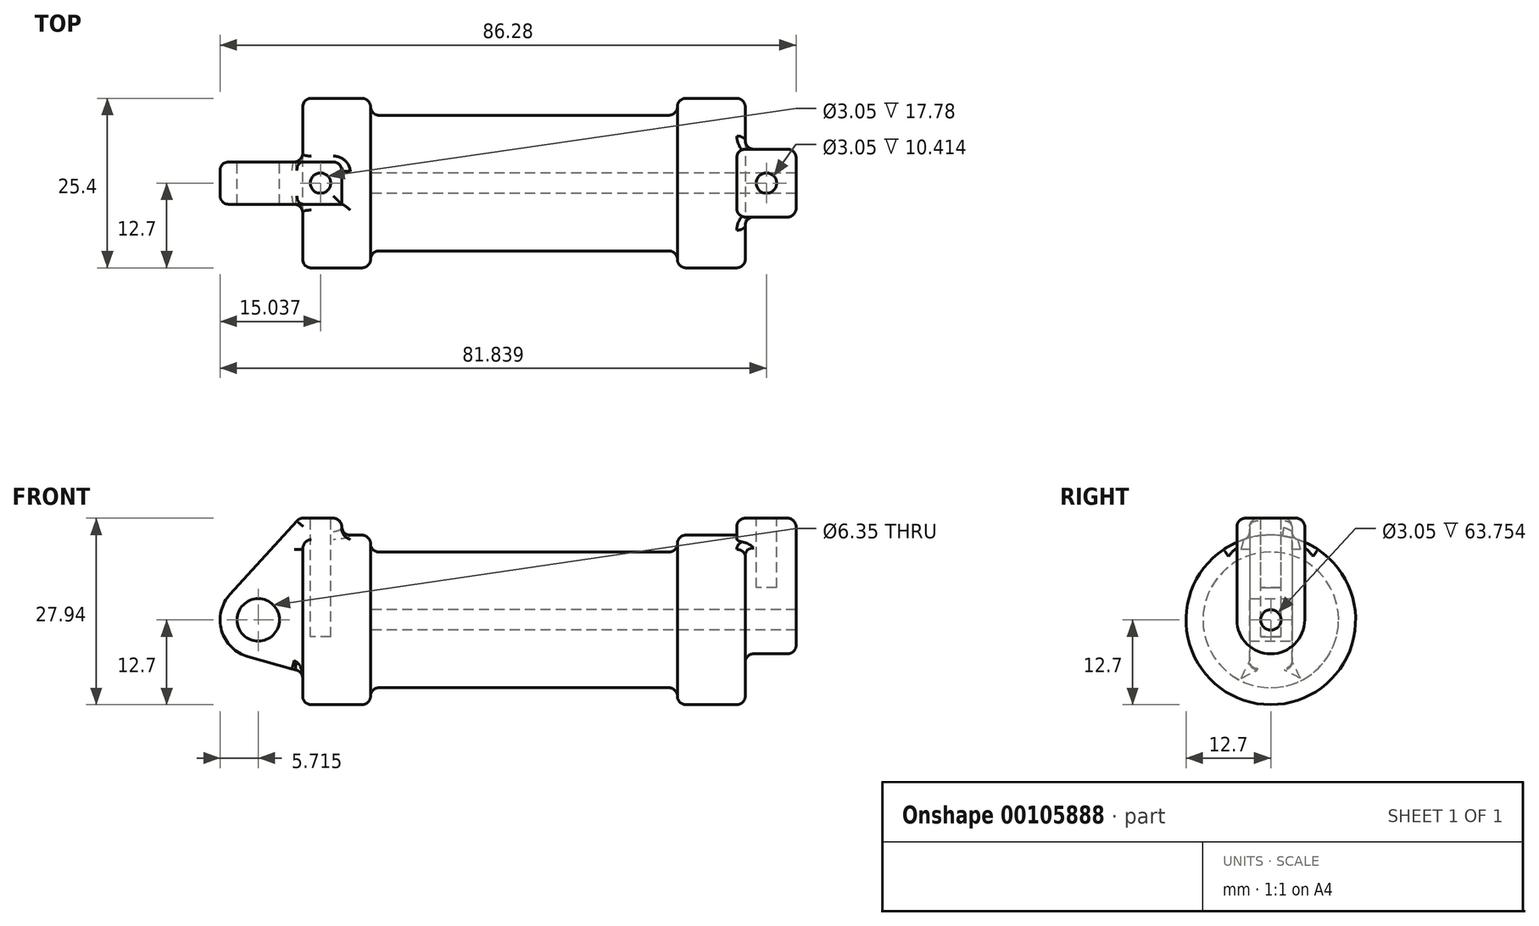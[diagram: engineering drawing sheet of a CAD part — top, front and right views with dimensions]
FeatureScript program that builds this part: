
annotation { "Feature Type Name" : "Feature", "Feature Type Description" : "" }
export const myFeature = defineFeature(function(context is Context, id is Id, definition is map)
    precondition{}
    {
        {
            var Q0;
            Q0=qCreatedBy(makeId("Front.planeOp"),FACE);
            var sketch = newSketch(context, id + "F0", { "sketchPlane" : qUnion([Q0])});
            skLineSegment(sketch, "E0", {"start": v(0, 0) * mm, "end": v(0, 12.7) * mm});
            skLineSegment(sketch, "E1", {"start": v(0, 12.7) * mm, "end": v(10.16, 12.7) * mm});
            skLineSegment(sketch, "E2", {"start": v(10.16, 12.7) * mm, "end": v(10.16, 10.16) * mm});
            skLineSegment(sketch, "E3", {"start": v(10.16, 10.16) * mm, "end": v(56.13, 10.16) * mm});
            skLineSegment(sketch, "E4", {"start": v(56.13, 10.16) * mm, "end": v(56.13, 12.7) * mm});
            skLineSegment(sketch, "E5", {"start": v(56.13, 12.7) * mm, "end": v(66.3, 12.7) * mm});
            skLineSegment(sketch, "E6", {"start": v(66.3, 12.7) * mm, "end": v(66.3, 0) * mm});
            skLineSegment(sketch, "E7", {"start": v(66.3, 0) * mm, "end": v(0, 0) * mm});
            skLineSegment(sketch, "E8", {"start": v(5.84, 15.24) * mm, "end": v(-0.5, 15.24) * mm});
            skLineSegment(sketch, "E9", {"start": v(-0.5, 15.24) * mm, "end": v(-10.88, 3.85) * mm});
            skLineSegment(sketch, "E10", {"start": v(0, 0) * mm, "end": v(-6.65, 0) * mm});
            skCircle(sketch, "E11", {"center": v(-6.65, 0) * mm, "radius": 5.72 * mm});
            skCircle(sketch, "E12", {"center": v(-6.65, 0) * mm, "radius": 3.18 * mm});
            skLineSegment(sketch, "E13", {"start": v(5.84, 15.24) * mm, "end": v(5.84, -9.4) * mm});
            skLineSegment(sketch, "E14", {"start": v(5.84, -9.4) * mm, "end": v(-8.18, -5.5) * mm});
            skSolve(sketch);
        }
        {
            var Q0;
            {var subQ0=sQuery(id+"F0.wireOp",EDGE,"E2");Q0=makeQuery(id+"F0.imprint","IMPRINT",FACE,{"disambiguationData":[TD([[makeQuery(id+"F0.imprint","IMPRINT",EDGE,{"derivedFrom":subQ0}),-1.0]])]});}
            var Q1;
            {var subQ0=sQuery(id+"F0.wireOp",EDGE,"E0");Q1=makeQuery(id+"F0.imprint","IMPRINT",FACE,{"disambiguationData":[TD([[makeQuery(id+"F0.imprint","IMPRINT",EDGE,{"derivedFrom":subQ0}),-1.0]])]});}
            var Q2;
            Q2=sQuery(id+"F0.wireOp",EDGE,"E7");
            revolve(context, id + "F1", {"entities" : qUnion([Q0, Q1]), "axis" : qUnion([Q2]), "revolveType" : RevolveType.FULL});
        }
        {
            var Q0;
            {var subQ3=sQuery(id+"F0.wireOp",EDGE,"E0");Q0=makeQuery(id+"F0.imprint","IMPRINT",FACE,{"disambiguationData":[TD([[makeQuery(id+"F0.imprint","IMPRINT",EDGE,{"derivedFrom":subQ3}),1.0]])]});}
            var Q1;
            {var subQ0=sQuery(id+"F0.wireOp",EDGE,"E0");Q1=makeQuery(id+"F0.imprint","IMPRINT",FACE,{"disambiguationData":[TD([[makeQuery(id+"F0.imprint","IMPRINT",EDGE,{"derivedFrom":subQ0}),-1.0]])]});}
            var Q2;
            {var subQ0=sQuery(id+"F0.wireOp",EDGE,"E14");Q2=makeQuery(id+"F0.imprint","IMPRINT",FACE,{"disambiguationData":[TD([[makeQuery(id+"F0.imprint","IMPRINT",EDGE,{"derivedFrom":subQ0}),-1.0]])]});}
            var Q3;
            {var subQ4=sQuery(id+"F0.wireOp",EDGE,"E12");Q3=makeQuery(id+"F0.imprint","IMPRINT",FACE,{"disambiguationData":[TD([[makeQuery(id+"F0.imprint","IMPRINT",EDGE,{"derivedFrom":subQ4}),-1.0]])]});}
            extrude(context, id + "F2", {"entities" : qUnion([Q0, Q1, Q2, Q3]), "operationType" : NewBodyOperationType.ADD, "endBound" : BoundingType.SYMMETRIC, "depth" : 6.35 * mm});
        }
        {
            var Q0;
            Q0=makeQuery(id+"F1.opRevolve","SWEPT_FACE",FACE,{"disambiguationData":[OSD([sQuery(id+"F0.wireOp",EDGE,"E6")])]});
            var sketch = newSketch(context, id + "F3", { "sketchPlane" : qUnion([Q0])});
            skCircle(sketch, "E15", {"center": v(0, 0) * mm, "radius": 1.52 * mm});
            skCircle(sketch, "E16", {"center": v(0, 0) * mm, "radius": 5.08 * mm});
            skLineSegment(sketch, "E17", {"start": v(5.08, 0) * mm, "end": v(5.08, 15.23) * mm});
            skLineSegment(sketch, "E18", {"start": v(-5.08, 0) * mm, "end": v(-5.08, 15.23) * mm});
            skLineSegment(sketch, "E19", {"start": v(-5.08, 15.23) * mm, "end": v(5.08, 15.23) * mm});
            skSolve(sketch);
        }
        {
            var Q0;
            {var subQ0=sQuery(id+"F3.wireOp",EDGE,"E19");Q0=makeQuery(id+"F3.imprint","IMPRINT",FACE,{"disambiguationData":[TD([[makeQuery(id+"F3.imprint","IMPRINT",EDGE,{"derivedFrom":subQ0}),-1.0]])]});}
            var Q1;
            {var subQ0=sQuery(id+"F3.wireOp",EDGE,"E17");var subQ1=sQuery(id+"F3.wireOp",EDGE,"E16");var subQ2=makeQuery(id+"F3.imprint","INTERSECT",VERTEX,{"derivedFrom":[subQ1,subQ0]});Q1=makeQuery(id+"F3.imprint","IMPRINT",FACE,{"disambiguationData":[TD([[makeQuery(id+"F3.imprint","IMPRINT",EDGE,{"disambiguationData":[TD([[subQ2,-1.0]])],"derivedFrom":subQ1}),-1.0]])]});}
            var Q2;
            Q2=makeQuery(id+"F3.imprint","IMPRINT",FACE,{"disambiguationData":[TD([[makeQuery(id+"F3.imprint","IMPRINT",EDGE,{"derivedFrom":sQuery(id+"F3.wireOp",EDGE,"E15")}),-1.0]])]});
            extrude(context, id + "F4", {"entities" : qUnion([Q0, Q1, Q2]), "operationType" : NewBodyOperationType.ADD, "depth" : 7.62 * mm});
        }
        {
            var Q0;
            Q0=makeQuery(id+"F4.opExtrude","CAP_FACE",FACE,{"disambiguationData":[OSD([sQuery(id+"F3.wireOp",EDGE,"E15"),sQuery(id+"F3.wireOp",EDGE,"E16"),sQuery(id+"F3.wireOp",EDGE,"E17"),sQuery(id+"F3.wireOp",EDGE,"E18"),sQuery(id+"F3.wireOp",EDGE,"E19")])],"isStart":true});
            extrude(context, id + "F5", {"entities" : qUnion([Q0]), "operationType" : NewBodyOperationType.ADD, "depth" : 1.27 * mm});
        }
        {
            var Q0;
            Q0=makeQuery(id+"F4.boolean.opBoolean","SPLIT",FACE,{"disambiguationData":[TD([makeQuery(id+"F4.opExtrude","SWEPT_FACE",FACE,{"disambiguationData":[OSD([sQuery(id+"F3.wireOp",EDGE,"E15")])]})])],"derivedFrom":makeQuery(id+"F1.opRevolve","SWEPT_FACE",FACE,{"disambiguationData":[OSD([sQuery(id+"F0.wireOp",EDGE,"E6")])]})});
            var Q1;
            Q1=makeQuery(id+"F1.opRevolve","SWEPT_FACE",FACE,{"disambiguationData":[OSD([sQuery(id+"F0.wireOp",EDGE,"E2")])]});
            extrude(context, id + "F6", {"entities" : qUnion([Q0]), "operationType" : NewBodyOperationType.REMOVE, "endBound" : BoundingType.UP_TO_SURFACE, "oppositeDirection" : true, "endBoundEntityFace" : qUnion([Q1]), "depth" : 25.4 * mm});
        }
        {
            var Q0;
            Q0=makeQuery(id+"F2.opExtrude","SWEPT_FACE",FACE,{"disambiguationData":[OSD([sQuery(id+"F0.wireOp",EDGE,"E8")])]});
            var sketch = newSketch(context, id + "F7", { "sketchPlane" : qUnion([Q0])});
            skCircle(sketch, "E20", {"center": v(2.67, 0) * mm, "radius": 1.52 * mm});
            skSolve(sketch);
        }
        {
            var Q0;
            {var subQ0=sQuery(id+"F3.wireOp",EDGE,"E19");Q0=makeQuery(id+"F5.boolean.opBoolean","MERGE",FACE,{"derivedFrom":[makeQuery(id+"F4.opExtrude","SWEPT_FACE",FACE,{"disambiguationData":[OSD([subQ0])]}),makeQuery(id+"F5.opExtrude","SWEPT_FACE",FACE,{"disambiguationData":[OSD([subQ0])]})]});}
            var sketch = newSketch(context, id + "F8", { "sketchPlane" : qUnion([Q0])});
            skCircle(sketch, "E21", {"center": v(69.47, 0) * mm, "radius": 1.52 * mm});
            skSolve(sketch);
        }
        {
            var Q0;
            Q0=makeQuery(id+"F7.imprint","IMPRINT",FACE,{"disambiguationData":[TD([[makeQuery(id+"F7.imprint","IMPRINT",EDGE,{"derivedFrom":sQuery(id+"F7.wireOp",EDGE,"E20")}),1.0]])]});
            extrude(context, id + "F9", {"entities" : qUnion([Q0]), "operationType" : NewBodyOperationType.REMOVE, "oppositeDirection" : true, "depth" : 17.78 * mm});
        }
        {
            var Q0;
            Q0=makeQuery(id+"F8.imprint","IMPRINT",FACE,{"disambiguationData":[TD([[makeQuery(id+"F8.imprint","IMPRINT",EDGE,{"derivedFrom":sQuery(id+"F8.wireOp",EDGE,"E21")}),1.0]])]});
            extrude(context, id + "F10", {"entities" : qUnion([Q0]), "operationType" : NewBodyOperationType.REMOVE, "oppositeDirection" : true, "depth" : 10.4 * mm});
        }
        {
            var Q0;
            Q0=makeQuery(id+"F1.opRevolve","SWEPT_EDGE",EDGE,{"disambiguationData":[OSD([sQuery(id+"F0.wireOp",EDGE,"E1"),sQuery(id+"F0.wireOp",EDGE,"E2")])]});
            var Q1;
            Q1=makeQuery(id+"F1.opRevolve","SWEPT_EDGE",EDGE,{"disambiguationData":[OSD([sQuery(id+"F0.wireOp",EDGE,"E2"),sQuery(id+"F0.wireOp",EDGE,"E3")])]});
            fillet(context, id + "F11", {"entities" : qUnion([Q0, Q1]), "radius" : 1.27 * mm, "tangentPropagation" : true, "allowEdgeOverflow" : false});
        }
        {
            var Q0;
            Q0=makeQuery(id+"F1.opRevolve","SWEPT_EDGE",EDGE,{"disambiguationData":[OSD([sQuery(id+"F0.wireOp",EDGE,"E4"),sQuery(id+"F0.wireOp",EDGE,"E5")])]});
            var Q1;
            Q1=makeQuery(id+"F1.opRevolve","SWEPT_EDGE",EDGE,{"disambiguationData":[OSD([sQuery(id+"F0.wireOp",EDGE,"E3"),sQuery(id+"F0.wireOp",EDGE,"E4")])]});
            fillet(context, id + "F12", {"entities" : qUnion([Q0, Q1]), "radius" : 1.27 * mm, "tangentPropagation" : true, "allowEdgeOverflow" : false});
        }
        {
            var Q0;
            Q0=makeQuery(id+"F2.opExtrude","SWEPT_EDGE",EDGE,{"disambiguationData":[OSD([sQuery(id+"F0.wireOp",EDGE,"E8"),sQuery(id+"F0.wireOp",EDGE,"E13")])]});
            var Q1;
            Q1=makeQuery(id+"F2.boolean.opBoolean","INTERSECT",EDGE,{"derivedFrom":[makeQuery(id+"F1.opRevolve","SWEPT_FACE",FACE,{"disambiguationData":[OSD([sQuery(id+"F0.wireOp",EDGE,"E1")])]}),makeQuery(id+"F2.opExtrude","CAP_FACE",FACE,{"disambiguationData":[OSD([sQuery(id+"F0.wireOp",EDGE,"E8"),sQuery(id+"F0.wireOp",EDGE,"E9"),sQuery(id+"F0.wireOp",EDGE,"E11"),sQuery(id+"F0.wireOp",EDGE,"E12"),sQuery(id+"F0.wireOp",EDGE,"E13"),sQuery(id+"F0.wireOp",EDGE,"E14")])],"isStart":false})]});
            var Q2;
            Q2=makeQuery(id+"F2.opExtrude","CAP_EDGE",EDGE,{"disambiguationData":[OSD([sQuery(id+"F0.wireOp",EDGE,"E8")])],"isStart":false});
            var Q3;
            Q3=makeQuery(id+"F2.opExtrude","CAP_EDGE",EDGE,{"disambiguationData":[OSD([sQuery(id+"F0.wireOp",EDGE,"E8")])],"isStart":true});
            var Q4;
            Q4=makeQuery(id+"F2.boolean.opBoolean","INTERSECT",EDGE,{"derivedFrom":[makeQuery(id+"F1.opRevolve","SWEPT_FACE",FACE,{"disambiguationData":[OSD([sQuery(id+"F0.wireOp",EDGE,"E1")])]}),makeQuery(id+"F2.opExtrude","SWEPT_FACE",FACE,{"disambiguationData":[OSD([sQuery(id+"F0.wireOp",EDGE,"E13")])]})]});
            var Q5;
            Q5=makeQuery(id+"F2.opExtrude","CAP_EDGE",EDGE,{"disambiguationData":[OSD([sQuery(id+"F0.wireOp",EDGE,"E13")])],"isStart":true});
            var Q6;
            Q6=makeQuery(id+"F2.boolean.opBoolean","INTERSECT",EDGE,{"derivedFrom":[makeQuery(id+"F1.opRevolve","SWEPT_FACE",FACE,{"disambiguationData":[OSD([sQuery(id+"F0.wireOp",EDGE,"E1")])]}),makeQuery(id+"F2.opExtrude","CAP_FACE",FACE,{"disambiguationData":[OSD([sQuery(id+"F0.wireOp",EDGE,"E8"),sQuery(id+"F0.wireOp",EDGE,"E9"),sQuery(id+"F0.wireOp",EDGE,"E11"),sQuery(id+"F0.wireOp",EDGE,"E12"),sQuery(id+"F0.wireOp",EDGE,"E13"),sQuery(id+"F0.wireOp",EDGE,"E14")])],"isStart":true})]});
            var Q7;
            Q7=makeQuery(id+"F1.opRevolve","SWEPT_EDGE",EDGE,{"disambiguationData":[OSD([sQuery(id+"F0.wireOp",EDGE,"E0"),sQuery(id+"F0.wireOp",EDGE,"E1")])]});
            var Q8;
            Q8=makeQuery(id+"F2.boolean.opBoolean","INTERSECT",EDGE,{"derivedFrom":[makeQuery(id+"F1.opRevolve","SWEPT_FACE",FACE,{"disambiguationData":[OSD([sQuery(id+"F0.wireOp",EDGE,"E0")])]}),makeQuery(id+"F2.opExtrude","CAP_FACE",FACE,{"disambiguationData":[OSD([sQuery(id+"F0.wireOp",EDGE,"E8"),sQuery(id+"F0.wireOp",EDGE,"E9"),sQuery(id+"F0.wireOp",EDGE,"E11"),sQuery(id+"F0.wireOp",EDGE,"E12"),sQuery(id+"F0.wireOp",EDGE,"E13"),sQuery(id+"F0.wireOp",EDGE,"E14")])],"isStart":true})]});
            var Q9;
            Q9=makeQuery(id+"F2.boolean.opBoolean","INTERSECT",EDGE,{"derivedFrom":[makeQuery(id+"F1.opRevolve","SWEPT_FACE",FACE,{"disambiguationData":[OSD([sQuery(id+"F0.wireOp",EDGE,"E0")])]}),makeQuery(id+"F2.opExtrude","SWEPT_FACE",FACE,{"disambiguationData":[OSD([sQuery(id+"F0.wireOp",EDGE,"E14")])]})]});
            var Q10;
            Q10=makeQuery(id+"F2.boolean.opBoolean","INTERSECT",EDGE,{"derivedFrom":[makeQuery(id+"F1.opRevolve","SWEPT_FACE",FACE,{"disambiguationData":[OSD([sQuery(id+"F0.wireOp",EDGE,"E0")])]}),makeQuery(id+"F2.opExtrude","CAP_FACE",FACE,{"disambiguationData":[OSD([sQuery(id+"F0.wireOp",EDGE,"E8"),sQuery(id+"F0.wireOp",EDGE,"E9"),sQuery(id+"F0.wireOp",EDGE,"E11"),sQuery(id+"F0.wireOp",EDGE,"E12"),sQuery(id+"F0.wireOp",EDGE,"E13"),sQuery(id+"F0.wireOp",EDGE,"E14")])],"isStart":false})]});
            var Q11;
            Q11=makeQuery(id+"F2.opExtrude","SWEPT_EDGE",EDGE,{"disambiguationData":[OSD([sQuery(id+"F0.wireOp",EDGE,"E8"),sQuery(id+"F0.wireOp",EDGE,"E9")])]});
            fillet(context, id + "F13", {"entities" : qUnion([Q0, Q1, Q2, Q3, Q4, Q5, Q6, Q7, Q8, Q9, Q10, Q11]), "radius" : 1.27 * mm, "tangentPropagation" : true, "allowEdgeOverflow" : false});
        }
        {
            var Q0;
            Q0=makeQuery(id+"F4.opExtrude","CAP_EDGE",EDGE,{"disambiguationData":[OSD([sQuery(id+"F3.wireOp",EDGE,"E19")])],"isStart":false});
            var Q1;
            {var subQ0=sQuery(id+"F3.wireOp",EDGE,"E19");var subQ1=sQuery(id+"F3.wireOp",EDGE,"E18");Q1=makeQuery(id+"F5.boolean.opBoolean","MERGE",EDGE,{"derivedFrom":[makeQuery(id+"F4.opExtrude","SWEPT_EDGE",EDGE,{"disambiguationData":[OSD([subQ1,subQ0])]}),makeQuery(id+"F5.opExtrude","SWEPT_EDGE",EDGE,{"disambiguationData":[OSD([subQ1,subQ0])]})]});}
            var Q2;
            Q2=makeQuery(id+"F5.opExtrude","CAP_EDGE",EDGE,{"disambiguationData":[OSD([sQuery(id+"F3.wireOp",EDGE,"E19")])],"isStart":false});
            var Q3;
            Q3=makeQuery(id+"F4.opExtrude","CAP_EDGE",EDGE,{"disambiguationData":[OSD([sQuery(id+"F3.wireOp",EDGE,"E18")])],"isStart":false});
            var Q4;
            Q4=makeQuery(id+"F5.opExtrude","CAP_EDGE",EDGE,{"disambiguationData":[OSD([sQuery(id+"F3.wireOp",EDGE,"E18")])],"isStart":false});
            var Q5;
            Q5=makeQuery(id+"F5.opExtrude","CAP_EDGE",EDGE,{"disambiguationData":[OSD([sQuery(id+"F3.wireOp",EDGE,"E17")])],"isStart":false});
            var Q6;
            {var subQ0=sQuery(id+"F3.wireOp",EDGE,"E17");var subQ1=sQuery(id+"F3.wireOp",EDGE,"E16");Q6=makeQuery(id+"F4.boolean.opBoolean","SPLIT",EDGE,{"disambiguationData":[TD([makeQuery(id+"F4.opExtrude","SWEPT_FACE",FACE,{"disambiguationData":[OSD([subQ1])]})])],"derivedFrom":makeQuery(id+"F4.opExtrude","CAP_EDGE",EDGE,{"disambiguationData":[OSD([subQ0])],"isStart":true})});}
            fillet(context, id + "F14", {"entities" : qUnion([Q0, Q1, Q2, Q3, Q4, Q5, Q6]), "radius" : 1.27 * mm, "tangentPropagation" : true, "allowEdgeOverflow" : false});
        }
        {
            var Q0;
            Q0=makeQuery(id+"F4.boolean.opBoolean","SPLIT",EDGE,{"disambiguationData":[OD(1.0)],"derivedFrom":makeQuery(id+"F1.opRevolve","SWEPT_EDGE",EDGE,{"disambiguationData":[OSD([sQuery(id+"F0.wireOp",EDGE,"E5"),sQuery(id+"F0.wireOp",EDGE,"E6")])]})});
            var Q1;
            Q1=makeQuery(id+"F2.opExtrude","CAP_EDGE",EDGE,{"disambiguationData":[OSD([sQuery(id+"F0.wireOp",EDGE,"E9")])],"isStart":false});
            var Q2;
            Q2=makeQuery(id+"F2.opExtrude","CAP_EDGE",EDGE,{"disambiguationData":[OSD([sQuery(id+"F0.wireOp",EDGE,"E9")])],"isStart":true});
            var Q3;
            {var subQ0=sQuery(id+"F3.wireOp",EDGE,"E19");var subQ1=sQuery(id+"F3.wireOp",EDGE,"E17");Q3=makeQuery(id+"F5.boolean.opBoolean","MERGE",EDGE,{"derivedFrom":[makeQuery(id+"F4.opExtrude","SWEPT_EDGE",EDGE,{"disambiguationData":[OSD([subQ1,subQ0])]}),makeQuery(id+"F5.opExtrude","SWEPT_EDGE",EDGE,{"disambiguationData":[OSD([subQ1,subQ0])]})]});}
            fillet(context, id + "F15", {"entities" : qUnion([Q0, Q1, Q2, Q3]), "radius" : 1.27 * mm, "tangentPropagation" : true, "allowEdgeOverflow" : false});
        }
    });
